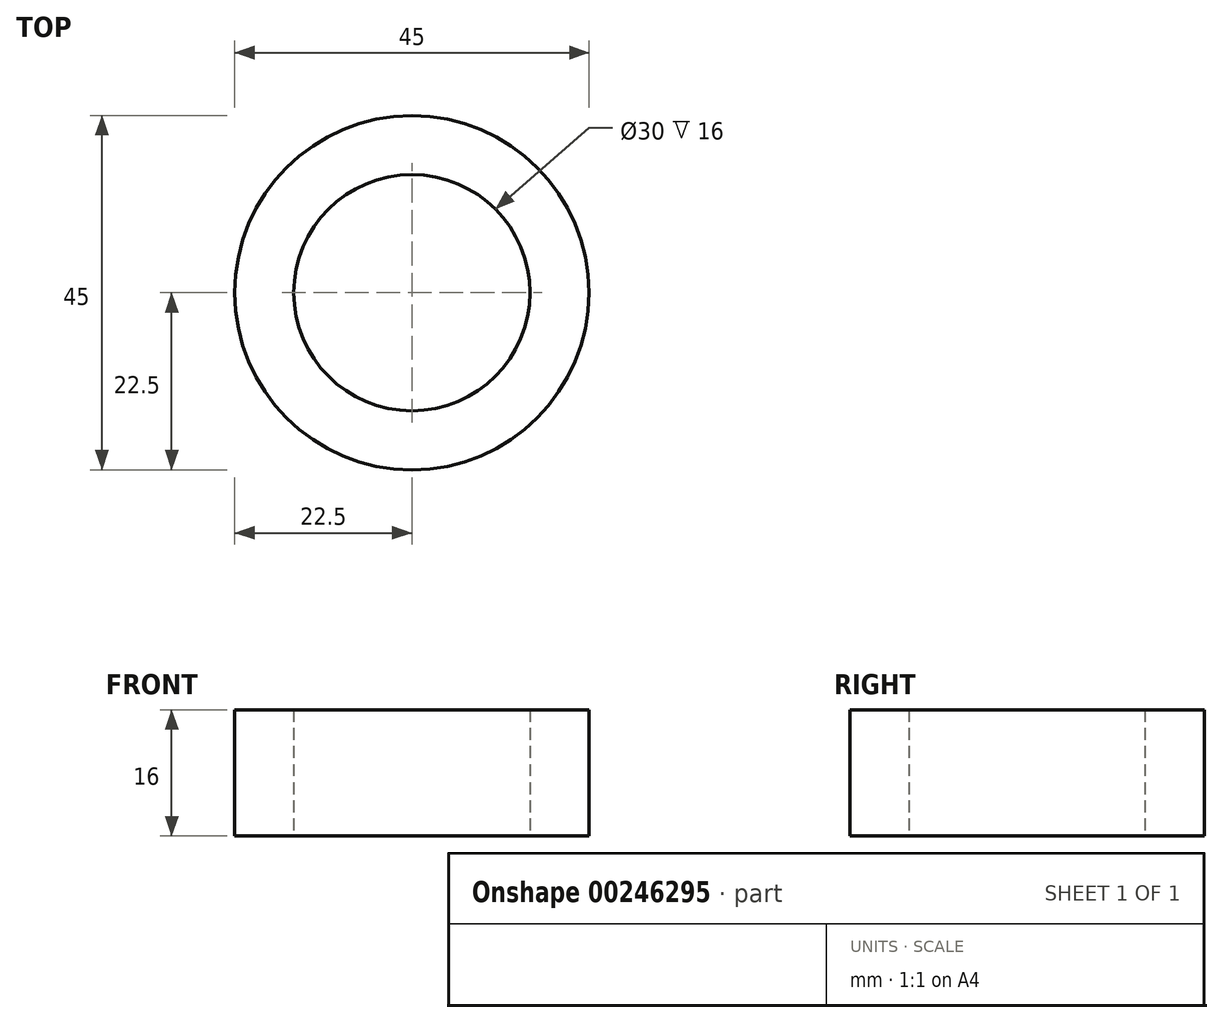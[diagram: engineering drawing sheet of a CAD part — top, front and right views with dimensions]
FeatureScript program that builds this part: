
annotation { "Feature Type Name" : "Feature", "Feature Type Description" : "" }
export const myFeature = defineFeature(function(context is Context, id is Id, definition is map)
    precondition{}
    {
        {
            var Q0;
            Q0=qCreatedBy(makeId("Top.planeOp"),FACE);
            var sketch = newSketch(context, id + "F0", { "sketchPlane" : qUnion([Q0])});
            skCircle(sketch, "E0", {"center": v(0, 0) * mm, "radius": 15 * mm});
            skCircle(sketch, "E1", {"center": v(0, 0) * mm, "radius": 22.5 * mm});
            skSolve(sketch);
        }
        {
            var Q0;
            Q0 = qSketchRegion(id + "F0", true);
            extrude(context, id + "F1", {"entities" : qUnion([Q0]), "depth" : 16 * mm});
        }
    });
